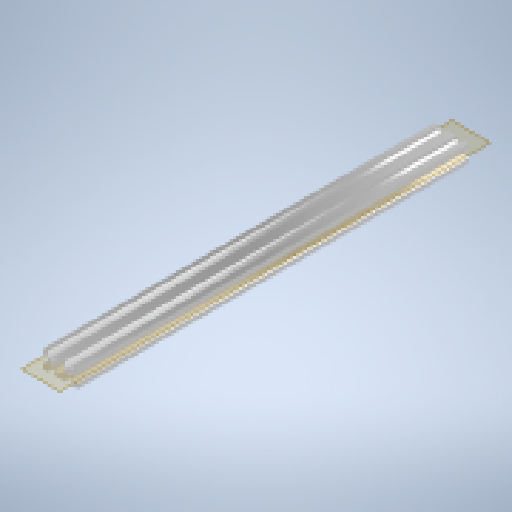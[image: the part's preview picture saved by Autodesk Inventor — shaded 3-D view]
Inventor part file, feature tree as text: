
AUTODESK INVENTOR PART (.ipt)
format: ipt  version: 2025.2 (Build 292293000, 293)  size: 383,488 bytes
history: native  units: in
note: dims shown in document units (in); Inventor stores cm internally (conversion verified against a paired STEP export)
features: extrude x1, sketch x1, other x1
ambient origin geometry x8: Origin, YZ Plane, XZ Plane, XY Plane, X Axis, Y Axis, Z Axis, Center Point
bodies: Solid1 (feature_tree)
feature tree (3):
  extrude  "Extrusion1"  [1 undecoded]
  sketch  "Sketch1"  dims[d0=1.9685in d1=0.0in]
  other  "Boss-Extrude1"
note: 1 required parameter value undecoded (feature->parameter linkage not recoverable at this tier; creation-order binding heuristic only, values carry confidence <= 0.55)
